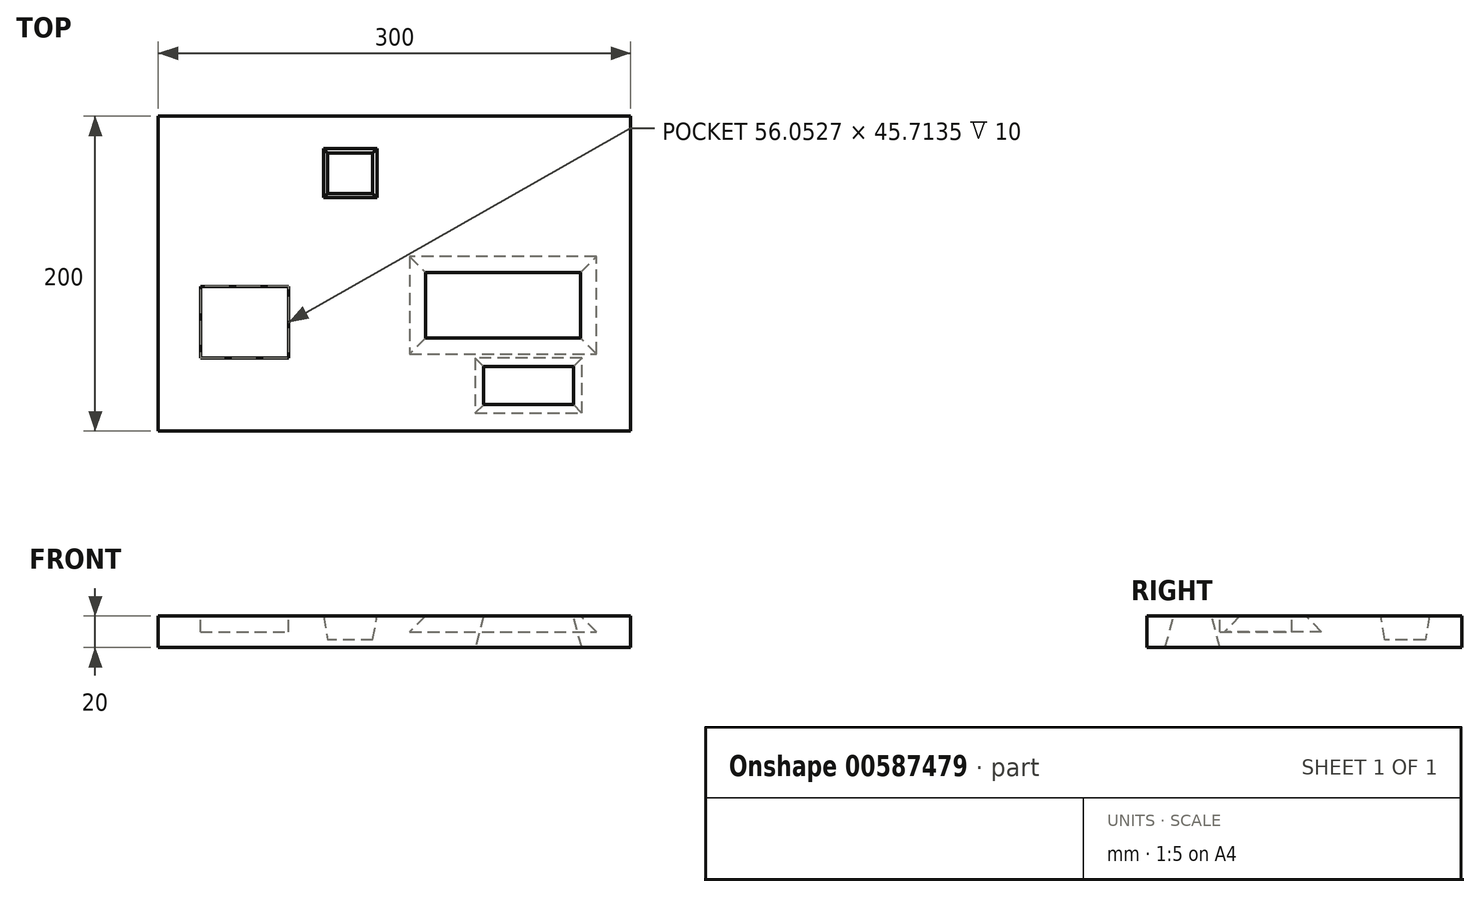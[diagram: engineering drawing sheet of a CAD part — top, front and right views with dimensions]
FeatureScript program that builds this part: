
annotation { "Feature Type Name" : "Feature", "Feature Type Description" : "" }
export const myFeature = defineFeature(function(context is Context, id is Id, definition is map)
    precondition{}
    {
        {
            var Q0;
            Q0=qCreatedBy(makeId("Top.planeOp"),FACE);
            var sketch = newSketch(context, id + "F0", { "sketchPlane" : qUnion([Q0])});
            skLineSegment(sketch, "E0.bottom", {"start": v(-130.1, -70.2) * mm, "end": v(169.9, -70.2) * mm});
            skLineSegment(sketch, "E0.top", {"start": v(-130.1, 129.8) * mm, "end": v(169.9, 129.8) * mm});
            skLineSegment(sketch, "E0.left", {"start": v(-130.1, -70.2) * mm, "end": v(-130.1, 129.8) * mm});
            skLineSegment(sketch, "E0.right", {"start": v(169.9, -70.2) * mm, "end": v(169.9, 129.8) * mm});
            skSolve(sketch);
        }
        {
            var Q0;
            Q0=makeQuery(id+"F0.imprint","IMPRINT",FACE,{"disambiguationData":[TD([[makeQuery(id+"F0.imprint","IMPRINT",EDGE,{"derivedFrom":sQuery(id+"F0.wireOp",EDGE,"E0.bottom")}),1.0]])]});
            extrude(context, id + "F1", {"entities" : qUnion([Q0]), "depth" : 20 * mm, "offsetDistance" : 25 * mm});
        }
        {
            var Q0;
            Q0=makeQuery(id+"F1.opExtrude","CAP_FACE",FACE,{"disambiguationData":[OSD([sQuery(id+"F0.wireOp",EDGE,"E0.bottom"),sQuery(id+"F0.wireOp",EDGE,"E0.top"),sQuery(id+"F0.wireOp",EDGE,"E0.left"),sQuery(id+"F0.wireOp",EDGE,"E0.right")])],"isStart":false});
            var sketch = newSketch(context, id + "F2", { "sketchPlane" : qUnion([Q0])});
            skLineSegment(sketch, "E1.bottom", {"start": v(-103.36, -23.9) * mm, "end": v(-47.3, -23.9) * mm});
            skLineSegment(sketch, "E1.top", {"start": v(-103.36, 21.8) * mm, "end": v(-47.3, 21.8) * mm});
            skLineSegment(sketch, "E1.left", {"start": v(-103.36, -23.9) * mm, "end": v(-103.36, 21.8) * mm});
            skLineSegment(sketch, "E1.right", {"start": v(-47.3, -23.9) * mm, "end": v(-47.3, 21.8) * mm});
            skSolve(sketch);
        }
        {
            var Q0;
            Q0=makeQuery(id+"F2.imprint","IMPRINT",FACE,{"disambiguationData":[TD([[makeQuery(id+"F2.imprint","IMPRINT",EDGE,{"derivedFrom":sQuery(id+"F2.wireOp",EDGE,"E1.bottom")}),1.0]])]});
            extrude(context, id + "F3", {"entities" : qUnion([Q0]), "operationType" : NewBodyOperationType.REMOVE, "oppositeDirection" : true, "depth" : 10 * mm, "offsetDistance" : 25 * mm});
        }
        {
            var Q0;
            Q0=makeQuery(id+"F1.opExtrude","CAP_FACE",FACE,{"disambiguationData":[OSD([sQuery(id+"F0.wireOp",EDGE,"E0.bottom"),sQuery(id+"F0.wireOp",EDGE,"E0.top"),sQuery(id+"F0.wireOp",EDGE,"E0.left"),sQuery(id+"F0.wireOp",EDGE,"E0.right")])],"isStart":false});
            var sketch = newSketch(context, id + "F4", { "sketchPlane" : qUnion([Q0])});
            skLineSegment(sketch, "E2.bottom", {"start": v(59.21, 62.74) * mm, "end": v(126.12, 62.74) * mm});
            skLineSegment(sketch, "E2.top", {"start": v(59.21, 96.76) * mm, "end": v(126.12, 96.76) * mm});
            skLineSegment(sketch, "E2.left", {"start": v(59.21, 62.74) * mm, "end": v(59.21, 96.76) * mm});
            skLineSegment(sketch, "E2.right", {"start": v(126.12, 62.74) * mm, "end": v(126.12, 96.76) * mm});
            skSolve(sketch);
        }
        {
            var Q0;
            Q0=makeQuery(id+"F4.imprint","IMPRINT",FACE,{"disambiguationData":[TD([[makeQuery(id+"F4.imprint","IMPRINT",EDGE,{"derivedFrom":sQuery(id+"F4.wireOp",EDGE,"E2.bottom")}),1.0]])]});
            extrude(context, id + "F5", {"entities" : qUnion([Q0]), "operationType" : NewBodyOperationType.ADD, "oppositeDirection" : true, "depth" : 10 * mm, "offsetDistance" : 25 * mm});
        }
        {
            var Q0;
            Q0=makeQuery(id+"F1.opExtrude","CAP_FACE",FACE,{"disambiguationData":[OSD([sQuery(id+"F0.wireOp",EDGE,"E0.bottom"),sQuery(id+"F0.wireOp",EDGE,"E0.top"),sQuery(id+"F0.wireOp",EDGE,"E0.left"),sQuery(id+"F0.wireOp",EDGE,"E0.right")])],"isStart":false});
            var sketch = newSketch(context, id + "F6", { "sketchPlane" : qUnion([Q0])});
            skLineSegment(sketch, "E3.bottom", {"start": v(39.47, -11.16) * mm, "end": v(138.07, -11.16) * mm});
            skLineSegment(sketch, "E3.top", {"start": v(39.47, 30.55) * mm, "end": v(138.07, 30.55) * mm});
            skLineSegment(sketch, "E3.left", {"start": v(39.47, -11.16) * mm, "end": v(39.47, 30.55) * mm});
            skLineSegment(sketch, "E3.right", {"start": v(138.07, -11.16) * mm, "end": v(138.07, 30.55) * mm});
            skSolve(sketch);
        }
        {
            var Q0;
            Q0=makeQuery(id+"F6.imprint","IMPRINT",FACE,{"disambiguationData":[TD([[makeQuery(id+"F6.imprint","IMPRINT",EDGE,{"derivedFrom":sQuery(id+"F6.wireOp",EDGE,"E3.bottom")}),1.0]])]});
            extrude(context, id + "F7", {"entities" : qUnion([Q0]), "operationType" : NewBodyOperationType.REMOVE, "oppositeDirection" : true, "depth" : 10 * mm, "offsetDistance" : 25 * mm, "hasDraft" : true, "draftAngle" : 45 * degree});
        }
        {
            var Q0;
            Q0=makeQuery(id+"F1.opExtrude","CAP_FACE",FACE,{"disambiguationData":[OSD([sQuery(id+"F0.wireOp",EDGE,"E0.bottom"),sQuery(id+"F0.wireOp",EDGE,"E0.top"),sQuery(id+"F0.wireOp",EDGE,"E0.left"),sQuery(id+"F0.wireOp",EDGE,"E0.right")])],"isStart":false});
            var sketch = newSketch(context, id + "F8", { "sketchPlane" : qUnion([Q0])});
            skLineSegment(sketch, "E4.bottom", {"start": v(-114.13, 116.98) * mm, "end": v(-81.5, 116.98) * mm});
            skLineSegment(sketch, "E4.top", {"start": v(-114.13, 85.81) * mm, "end": v(-81.5, 85.81) * mm});
            skLineSegment(sketch, "E4.left", {"start": v(-114.13, 116.98) * mm, "end": v(-114.13, 85.81) * mm});
            skLineSegment(sketch, "E4.right", {"start": v(-81.5, 116.98) * mm, "end": v(-81.5, 85.81) * mm});
            skSolve(sketch);
        }
        {
            var Q0;
            Q0=makeQuery(id+"F8.imprint","IMPRINT",FACE,{"disambiguationData":[TD([[makeQuery(id+"F8.imprint","IMPRINT",EDGE,{"derivedFrom":sQuery(id+"F8.wireOp",EDGE,"E4.bottom")}),-1.0]])]});
            extrude(context, id + "F9", {"entities" : qUnion([Q0]), "operationType" : NewBodyOperationType.ADD, "oppositeDirection" : true, "depth" : 10 * mm, "offsetDistance" : 25 * mm, "hasDraft" : true, "draftAngle" : 20 * degree});
        }
        {
            var Q0;
            Q0=makeQuery(id+"F1.opExtrude","CAP_FACE",FACE,{"disambiguationData":[OSD([sQuery(id+"F0.wireOp",EDGE,"E0.bottom"),sQuery(id+"F0.wireOp",EDGE,"E0.top"),sQuery(id+"F0.wireOp",EDGE,"E0.left"),sQuery(id+"F0.wireOp",EDGE,"E0.right")])],"isStart":false});
            var sketch = newSketch(context, id + "F10", { "sketchPlane" : qUnion([Q0])});
            skLineSegment(sketch, "E5.bottom", {"start": v(-25.21, 109.18) * mm, "end": v(8.77, 109.18) * mm});
            skLineSegment(sketch, "E5.top", {"start": v(-25.21, 78.11) * mm, "end": v(8.77, 78.11) * mm});
            skLineSegment(sketch, "E5.left", {"start": v(-25.21, 109.18) * mm, "end": v(-25.21, 78.11) * mm});
            skLineSegment(sketch, "E5.right", {"start": v(8.77, 109.18) * mm, "end": v(8.77, 78.11) * mm});
            skSolve(sketch);
        }
        {
            var Q0;
            Q0=makeQuery(id+"F10.imprint","IMPRINT",FACE,{"disambiguationData":[TD([[makeQuery(id+"F10.imprint","IMPRINT",EDGE,{"derivedFrom":sQuery(id+"F10.wireOp",EDGE,"E5.bottom")}),-1.0]])]});
            extrude(context, id + "F11", {"entities" : qUnion([Q0]), "operationType" : NewBodyOperationType.REMOVE, "oppositeDirection" : true, "depth" : 15 * mm, "offsetDistance" : 25 * mm, "hasDraft" : true, "draftAngle" : 10 * degree, "draftPullDirection" : true});
        }
        {
            var Q0;
            Q0=makeQuery(id+"F1.opExtrude","CAP_FACE",FACE,{"disambiguationData":[OSD([sQuery(id+"F0.wireOp",EDGE,"E0.bottom"),sQuery(id+"F0.wireOp",EDGE,"E0.top"),sQuery(id+"F0.wireOp",EDGE,"E0.left"),sQuery(id+"F0.wireOp",EDGE,"E0.right")])],"isStart":false});
            var sketch = newSketch(context, id + "F12", { "sketchPlane" : qUnion([Q0])});
            skLineSegment(sketch, "E6.bottom", {"start": v(76.5, -29.2) * mm, "end": v(133.48, -29.2) * mm});
            skLineSegment(sketch, "E6.top", {"start": v(76.5, -53.41) * mm, "end": v(133.48, -53.41) * mm});
            skLineSegment(sketch, "E6.left", {"start": v(76.5, -29.2) * mm, "end": v(76.5, -53.41) * mm});
            skLineSegment(sketch, "E6.right", {"start": v(133.48, -29.2) * mm, "end": v(133.48, -53.41) * mm});
            skSolve(sketch);
        }
        {
            var Q0;
            Q0=makeQuery(id+"F12.imprint","IMPRINT",FACE,{"disambiguationData":[TD([[makeQuery(id+"F12.imprint","IMPRINT",EDGE,{"derivedFrom":sQuery(id+"F12.wireOp",EDGE,"E6.bottom")}),-1.0]])]});
            extrude(context, id + "F13", {"entities" : qUnion([Q0]), "operationType" : NewBodyOperationType.REMOVE, "oppositeDirection" : true, "depth" : 25 * mm, "offsetDistance" : 25 * mm, "hasDraft" : true, "draftAngle" : 15 * degree});
        }
    });
